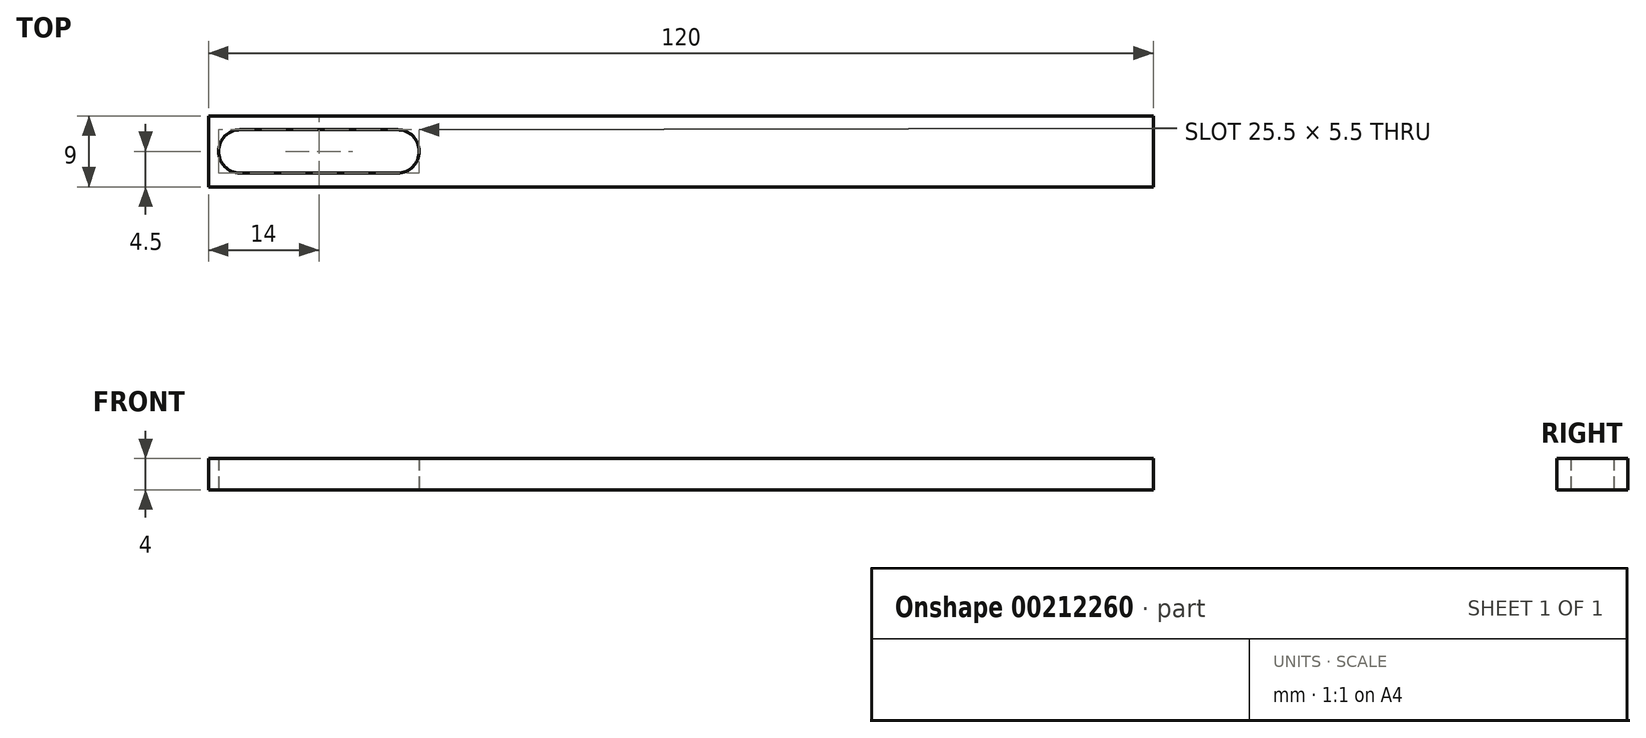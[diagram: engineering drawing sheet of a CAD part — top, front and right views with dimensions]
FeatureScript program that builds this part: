
annotation { "Feature Type Name" : "Feature", "Feature Type Description" : "" }
export const myFeature = defineFeature(function(context is Context, id is Id, definition is map)
    precondition{}
    {
        {
            var Q0;
            Q0=qCreatedBy(makeId("Top.planeOp"),FACE);
            var sketch = newSketch(context, id + "F0", { "sketchPlane" : qUnion([Q0])});
            skLineSegment(sketch, "E0.bottom", {"start": v(-120, 0) * mm, "end": v(0, 0) * mm});
            skLineSegment(sketch, "E0.top", {"start": v(-120, 9) * mm, "end": v(0, 9) * mm});
            skLineSegment(sketch, "E0.left", {"start": v(-120, 0) * mm, "end": v(-120, 9) * mm});
            skLineSegment(sketch, "E0.right", {"start": v(0, 0) * mm, "end": v(0, 9) * mm});
            skCircle(sketch, "E1", {"center": v(-116, 4.5) * mm, "radius": 2.75 * mm});
            skCircle(sketch, "E2", {"center": v(-96, 4.5) * mm, "radius": 2.75 * mm});
            skLineSegment(sketch, "E3", {"start": v(-120, 4.5) * mm, "end": v(0, 4.5) * mm, "construction": true});
            skLineSegment(sketch, "E4", {"start": v(-116, 1.75) * mm, "end": v(-96, 1.75) * mm});
            skLineSegment(sketch, "E5", {"start": v(-116, 7.25) * mm, "end": v(-96, 7.25) * mm});
            skSolve(sketch);
        }
        {
            var Q0;
            Q0=makeQuery(id+"F0.imprint","IMPRINT",FACE,{"disambiguationData":[TD([[makeQuery(id+"F0.imprint","IMPRINT",EDGE,{"derivedFrom":sQuery(id+"F0.wireOp",EDGE,"E0.bottom")}),1.0]])]});
            extrude(context, id + "F1", {"entities" : qUnion([Q0]), "depth" : 4 * mm});
        }
    });
